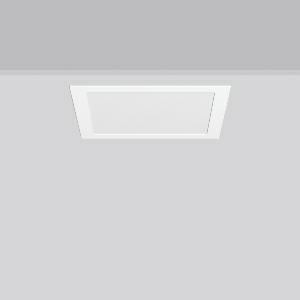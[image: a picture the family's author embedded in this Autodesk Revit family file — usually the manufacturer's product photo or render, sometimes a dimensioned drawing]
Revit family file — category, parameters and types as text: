
# Revit family: toledo_flat_square_e_672244_002_89_d364
name_source: partatom
category: Lighting Fixtures
units: mm (PartAtom-declared; Revit-internal decimal feet)

## family parameters
Cut with Voids When Loaded = No
Host = Face
Light Source = No
Part Type = Normal
Room Calculation Point = No
Round Connector Dimension = Use Diameter
Shared = No

## types (1)
- TOLEDO FLAT square E (1 x LED Modul 830, 2050 lm, 3000)
    Apparent Load = 23 VA
    CIE Flux Codes = 48 80 96 100 100
    Color Rendering = 80
    Color Temperature = 3000
    Default Elevation = 1800 mm
    Description = Series: TOLEDO FLAT square
Square recessed downlight. For escape route illumination. Housing: die-cast aluminium, powder-coated. Lightguide and diffuser made of non-yellowing plastic (PMMA). Diffuser opal matt plastic. Ceiling installation with spring system. Including separate LED converter with connecting cable 250 mm. Suitable for connection to central battery systems. With AC Control monitoring module for LUXIFAIR central battery units. External driver with simple plug-in locking system. 
Colour: white
Length: 300 mm
Width: 300 mm
Height: 3 mm
Cut-out length: 280 mm
Cut-out width: 280 mm
Recess height: 40 mm
Luminaire: recess height: 37-57 mm
Weight: 1.97 kg
Operating mode: maintained power mode
Lamp: LED
Socket: without socket
Colour temperature: 3000K
Colour rendering index (CRI): 80
System power: 23 W
Rated luminous flux: 2050 lm
Luminous flux, emergency: 2050 lm
System power, emergency: 23 W
Control gear: Regulated power supply
Protection class: I
Type of protection: IP 54
    Height = 0 mm  [stored 0 ft]
    Lamp = 1 x LED Modul 830
    Lamp Light Flux = 2050 lm
    Lamp count = 1
    Length = 300 mm
    Lifetime = 50000 h
    Luminous efficacy = 89 lm/W
    Manufacturer = RZB
    ModVariant = No
    Model = 672244.002.89
    Mounting Place = Ceiling
    Mounting Type = Recessed
    Number of Poles = 1
    OnlyDefault = Yes
    Power Factor = 1
    Product Name = TOLEDO FLAT square E
    Product group = Recessed downlights
    ProductGroupID = 402
    Protection Class = Protection class I
    Protection Degree = IP 40
    RLX_Detail_Level = 1
    RLX_Emergency_Light_Flux = 2050 lm
    RLX_Emergency_Type = 3
    RLX_Emergency_Type_DB = Yes
    RlxData = <blob elided: 12949 chars, md5=6012bc67>
    Socket = socket
    Standby Power = 0 W
    System Light Flux = 2050 lm
    System Power = 23 W
    Type Comments = Product without accessories
    Type Image = 901488.002.jpg
    URL = http://relux.com
    VarID = ---
    Voltage = 230 V
    Voltage Range = 220-240 V
    Weight = 0.00 kg
    Width = 300 mm

note: [stored X ft] marks values corroborated as IEEE doubles in the binary element streams (Revit-internal decimal feet)

## geometry (parser evidence)
native form markers: Sweep x9
no freeform markers — native parametric forms only
